# Revit family: Domotics-DomesticRanges-GEWISS-CHORUS_COMMAND-TWO-WAY_SWITCH_05M
name_source: partatom
category: Apparecchi elettrici
revit_build: Autodesk Revit 2016 (Build: 20161004_0715(x64)
units: mm (PartAtom-declared; Revit-internal decimal feet)

## family parameters
Condiviso = Sì
Host = Superficie
Mantenere orientamento annotazione = Sì
Numero OmniClass = 23.80.50.11.14
Punto di calcolo locali = No
Quota connettore circolare = Usa diametro
Taglio con vuoti quando caricato = Sì
Tipo di parte = Normale
Titolo OmniClass = Switches

## types (3) — shared parameters
Breaking capacity: = 1.25 In (200 position changes)
Button key = Neutral
Carico apparente = 0 VA
Catalogue = DOMOTICS
Catalogue Range = CHORUS - DOMESTIC RANGE
Category = Two-way switch
Description: = 1P - 10AX
Electrocod = 0130
Glow Wire Test = 850°C
IDF = cabf7e10-7a13-426c-a593-8463eb0fb710
IDT = 787a1ab5-a9e8-46ba-8a65-4ed75fbb2ff2
Immagine tipo = GW14061.jpg
Insulation resistance = > 5 MOhm
Larghezza pulsante = 12 mm  [stored 0.0393701 ft]
N. poli = 1
No. Chorus modules = 1/2
Produttore = GEWISS S.p.A.
Prolonged operation (no.of position changes) = 40.000 at In 250 V ac cosÃ˜=0,6
Prospetto di default = 1219 mm
Resistance at test voltage = 2000 V at 50 Hz for 1 minute
SEO = 2 way switch
Simbolo_ = SIMBOLO DEVIATORI : DEV1P
Standard; = EN 60669-1
Technical sheet = https://www.gewiss.com
Terminal grip on cable traction = > 50 N
Terminal tightening capacity flexible cables (mm2) = min. 0,75 - max. 2x4
Terminal tightening capacity rigid cables (mm2) = min. 0,5 - max. 2x2,5
Thermo-pressure with ball = 125
Tipo_ = CHORUS DEVIATORI 05M_BASE : GW14054 - Titanio
Type = General
URL = https://www.gewiss.com
Version file RFA = 19.0
Volt = 0 V
Voltage: = 250 V ac
Wiring terminals = With screw

## per-type parameters (varying)
| type | Colour | Descrizione | EAN code | Modello |
| GW12061 - Black | Black | 2-WAY SWITCH, 1/2M 1P 10AX BLACK | 8011564269347 | GW12061 |
| GW10061 - White | White | 2-WAY SWITCH, 1/2M 1P 10AX WHITE | 8011564261013 | GW10061 |
| GW14061 - Titanium | Titanium | 2-WAY SWITCH, 1/2M 1P 10AX TITANIUM | 8011564265585 | GW14061 |

note: source unit labels omitted for Thermo-pressure with ball — the stored unit's dimension contradicts the parameter name (converter mislabeling)

note: [stored X ft] marks values corroborated as IEEE doubles in the binary element streams (Revit-internal decimal feet)

## geometry (parser evidence)
native form markers: Sweep x1
no freeform markers — native parametric forms only
